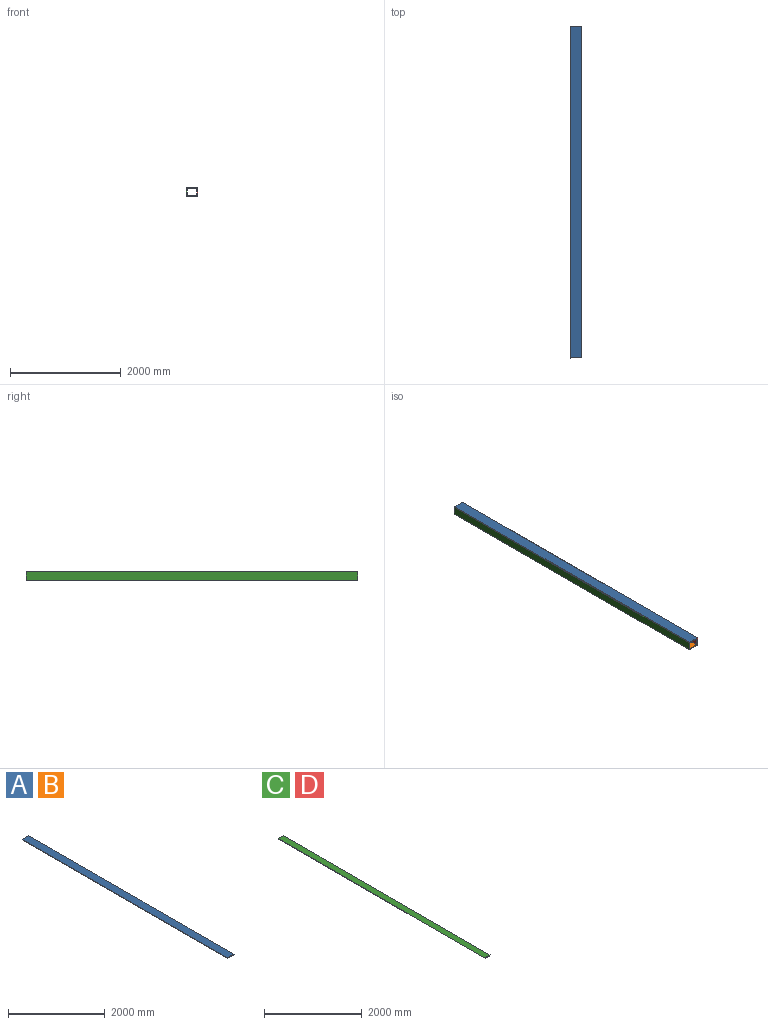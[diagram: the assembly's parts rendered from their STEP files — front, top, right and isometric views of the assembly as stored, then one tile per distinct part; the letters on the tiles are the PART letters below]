
ASSEMBLY  parts=4 mates=7
PART A: 6 faces, bbox 200.2x5994.4x19.1 mm
  f0: plane 5994.4x173.02mm, normal (0,0,-1), area 1037179.1mm2, adj f1,f3,f4,f5
  f1: plane 5994.4x19.05mm, normal (0.81,0,-0.58), area 140181.3mm2, adj f0,f2,f4,f5
  f2: plane 5994.4x200.15mm, normal (0,0,1), area 1199791.1mm2, adj f1,f3,f4,f5
  f3: plane 5994.4x19.05mm, normal (-0.81,0,-0.58), area 140181.3mm2, adj f0,f2,f4,f5
  f4: plane 200.15x19.05mm, normal (0,-1,0), area 3554.5mm2, adj f0,f1,f2,f3
  f5: plane 200.15x19.05mm, normal (0,1,0), area 3554.5mm2, adj f0,f1,f2,f3
PART B: same geometry as A
PART C: 6 faces, bbox 149.4x5994.4x19.1 mm
  f0: plane 5994.4x122.22mm, normal (0,0,-1), area 732663.5mm2, adj f1,f3,f4,f5
  f1: plane 5994.4x19.05mm, normal (0.81,0,-0.58), area 140181.3mm2, adj f0,f2,f4,f5
  f2: plane 5994.4x149.35mm, normal (0,0,1), area 895275.6mm2, adj f1,f3,f4,f5
  f3: plane 5994.4x19.05mm, normal (-0.81,0,-0.58), area 140181.3mm2, adj f0,f2,f4,f5
  f4: plane 149.35x19.05mm, normal (0,-1,0), area 2586.8mm2, adj f0,f1,f2,f3
  f5: plane 149.35x19.05mm, normal (0,1,0), area 2586.8mm2, adj f0,f1,f2,f3
PART D: same geometry as C
PLACE A t=(384.07,80.97,-309.31)mm
PLACE B rot(axis=(1,0,0),180deg) t=(385.33,-5913.43,-474.41)mm
PLACE C rot(axis=(0,-1,0),90deg) t=(454.31,80.97,-514.94)mm
PLACE D rot(axis=(0,1,0),90deg) t=(511.43,80.97,-269.01)mm
MATE parallel A.f4 <-> B.f5  axis (0,-1,0) through (483.06,-5913.43,-318.61)mm
MATE planar A.f4 <-> D.f4  axis (0,-1,0) through (483.06,-5913.43,-318.61)mm
MATE parallel A.f4 <-> C.f4  axis (0,-1,0) through (483.06,-5913.43,-318.61)mm
MATE planar D.f4 <-> B.f5  axis (0,-1,0) through (581.62,-5913.43,-391.72)mm
MATE parallel B.f0 <-> A.f0  axis (0,0,1) through (484.32,-2916.23,-455.36)mm
MATE parallel D.f0 <-> C.f0  axis (-1,0,0) through (571.77,-2916.23,-391.72)mm
MATE planar A.f4 <-> C.f4  axis (0,-1,0) through (483.06,-5913.43,-318.61)mm
